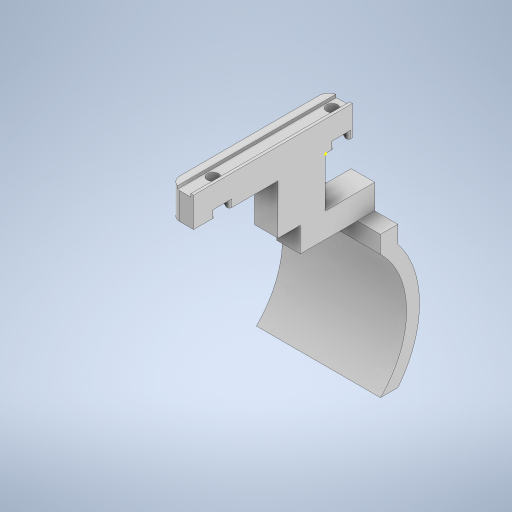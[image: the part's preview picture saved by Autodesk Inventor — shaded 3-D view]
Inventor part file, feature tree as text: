
AUTODESK INVENTOR PART (.ipt)
format: ipt  version: 2024 (Build 280153000, 153)  size: 364,544 bytes
history: native  units: in
note: dims shown in document units (in); Inventor stores cm internally (conversion verified against a paired STEP export)
features: sketch x10, extrude x7, projected_geometry x4, fillet x2, sweep x1
ambient origin geometry x8: Origin, YZ Plane, XZ Plane, XY Plane, X Axis, Y Axis, Z Axis, Center Point
bodies: Solid1 (feature_tree)
feature tree (24):
  extrude  "Extrusion1"  Depth=2.5197in
  extrude  "Extrusion2"  Depth=1.8898in
  extrude  "Extrusion3"  Depth=0.4724in TaperAngle=0.0deg
  fillet  "Fillet1"  Radius=0.0433in
  fillet  "Fillet2"  Radius=0.2126in
  extrude  "Extrusion19"  Depth=0.4724in TaperAngle=0.0deg
  extrude  "Extrusion21"  Depth=0.1181in TaperAngle=0.0deg
  sketch  "Sketch41"  dims[d17=0.1772in d18=0.0394in]
  extrude  "Extrusion22"  Depth=0.0394in
  sweep  "Sweep3"
  extrude  "Extrusion25"  Depth=0.748in
  sketch  "Sketch1"  dims[d1=0.374in d2=2.5197in]
  sketch  "Sketch2"  dims[d3=0.1772in d4=1.8898in]
  sketch  "Sketch3"  dims[d6=0.1457in d7=0.4724in d8=0.0in d9=0.0433in d10=0.2126in]
  projected_geometry  "Projected Loop2"
  projected_geometry  "Projected Loop3"
  projected_geometry  "Projected Loop4"
  projected_geometry  "Projected Loop5"
  sketch  "Sketch28"  dims[d11=0.0472in d12=0.4724in d13=0.0in]
  sketch  "Sketch40"  dims[d14=0.2953in d15=0.1181in d16=0.0in]
  sketch  "Sketch42"  dims[d19=0.1575in d76=0.4724in]
  sketch  "Sketch43"  dims[d107=0.102in d108=0.748in]
  sketch  "Sketch44"  dims[d109=0.7874in d110=0.0in]
  sketch  "Sketch54"  dims[d130=0.7874in d131=1.1811in d132=0.3937in d133=0.0in d134=1.2283in d135=180.0deg d136=0.2756in d137=1.9685in d138=0.2756in d139=0.2756in d140=0.0in d141=1.9685in d142=1.378in d143=0.0in d144=0.0in d154=4.1063in d155=0.0in d42=0.0197in d43=0.0344in d44=0.0197in d45=0.0344in d46=0.0in d47=0.0in d48=0.0in d49=0.0in d50=0.0in d51=0.0in d52=0.0in d53=0.0in d55=0.0197in d56=0.0344in d57=0.0197in d58=0.0344in d60=0.0197in d61=0.0344in d62=0.0197in d63=0.0344in d72=0.0197in d73=0.0344in d74=0.0197in d75=0.0344in]
